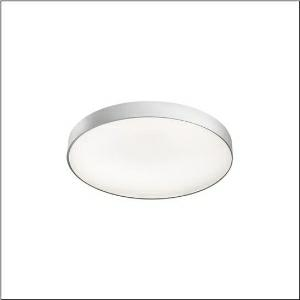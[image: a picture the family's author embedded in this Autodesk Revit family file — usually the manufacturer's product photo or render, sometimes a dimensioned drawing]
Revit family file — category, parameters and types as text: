
# Revit family: round_21_m_51mr36nd0321s
name_source: partatom
category: Lighting Fixtures
units: mm (PartAtom-declared; Revit-internal decimal feet)

## family parameters
Cut with Voids When Loaded = No
Host = Face
Light Source = No
Part Type = Normal
Room Calculation Point = No
Round Connector Dimension = Use Diameter
Shared = No

## types (1)
- Round 21 M (1 x LED, 7170 lm, 54.6 W, 3000K)
    Apparent Load = 55 VA
    CIE Flux Codes = 66 90 98 84 100
    Color Rendering = 80
    Color Temperature = 3000K
    Default Elevation = 1800 mm
    Description = Round 21 M, wall and ceiling luminaire, primary optical cover: micro prismatic cover, of PMMA, transparent, CAT 2 (L<= 3000cd/m²), light emission: direct/indirect distribution, primary light characteristic: symmetric, installation type: surface-mounted, suspended mounting, LED, rated luminous flux: 7.130lm, luminous efficacy: 131lm/W, light colour: 830, colour temperature: 3000K, control gear: DALI 2, with terminal, 5-pole, mains connection: 230V, AC, 50/60Hz, rated input power: 54.6W, housing, of aluminium, coated, silver, diameter: 600mm, height: 62mm, protection rating (complete): IP40, insulation class (complete): insulation class I (protective earthing), certification: CE, impact resistance: IK04, permissible operating ambient temperature: -10..+35°C, packaging unit: 1 piece
    Height = 87 mm
    Lamp = 1 x LED
    Lamp Light Flux = 7170 lm
    Lamp Power = 54.6 W
    Lamp count = 1
    Length = 600 mm
    Luminous efficacy = 131 lm/W
    Manufacturer = Siteco
    ModVariant = No
    Model = 51MR36ND0321S
    Mounting Place = Ceiling
    Mounting Type = Surface mounted
    Number of Poles = 1
    OnlyDefault = Yes
    Power Factor = 1
    Product Name = Round 21 M
    Product group = wall and ceiling luminaire
    ProductGroupID = 304
    Protection Class = Protection class I
    Protection Degree = IP 40
    RLX_Detail_Level = 1
    RLX_Emergency_Light_Flux = 0 lm
    RLX_Emergency_Type = 0
    RLX_Emergency_Type_DB = No
    RlxData = <blob elided: 19009 chars, md5=3372ad42>
    Socket = socket
    Standby Power = 0 W
    System Light Flux = 7170 lm
    System Power = 55 W
    Type Comments = Product without accessories
    Type Image = l_1258301.jpg
    URL = http://relux.com
    VarID = ---
    Voltage = 0 V
    Weight = 0.00 kg
    Width = 0 mm  [stored 0 ft]

note: [stored X ft] marks values corroborated as IEEE doubles in the binary element streams (Revit-internal decimal feet)

## geometry (parser evidence)
native form markers: Blend x4, Sweep x12
no freeform markers — native parametric forms only
